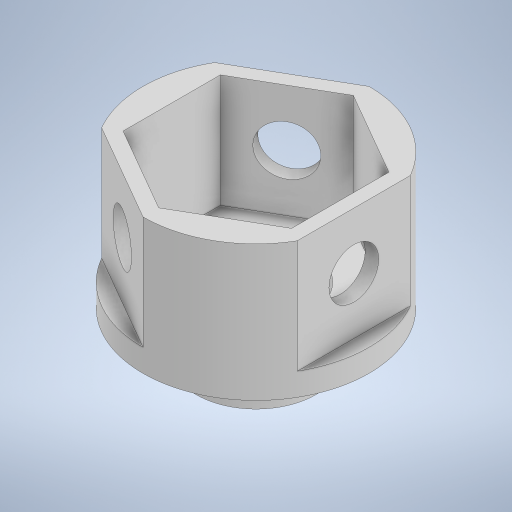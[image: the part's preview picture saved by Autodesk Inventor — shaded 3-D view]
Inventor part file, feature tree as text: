
AUTODESK INVENTOR PART (.ipt)
format: ipt  version: 2023 (Build 270158000, 158)  size: 289,792 bytes
history: native  units: in
note: dims shown in document units (in); Inventor stores cm internally (conversion verified against a paired STEP export)
features: extrude x7, sketch x7, pattern_circular x1
ambient origin geometry x8: Origin, YZ Plane, XZ Plane, XY Plane, X Axis, Y Axis, Z Axis, Center Point
bodies: Solid1 (feature_tree)
feature tree (15):
  extrude  "Extrusion1"  Depth=0.1969in TaperAngle=0.0deg
  extrude  "Extrusion2"  Depth=0.9843in TaperAngle=0.0deg
  extrude  "Extrusion3"  Depth=0.9843in TaperAngle=0.0deg
  extrude  "Extrusion4"  Depth=0.4921in
  extrude  "Extrusion5"  Depth=0.4921in
  pattern_circular  "Circular Pattern1"  Count=3 Angle=360.0deg
  extrude  "Extrusion6"  Depth=0.3937in
  extrude  "Extrusion7"  Depth=0.3937in
  sketch  "Sketch1"  dims[d0=1.9685in d1=0.1969in d2=0.0in]
  sketch  "Sketch2"  dims[d3=0.9843in d4=0.0in d5=0.9843in d6=0.0in]
  sketch  "Sketch3"  dims[d7=0.1181in d8=0.9843in d9=0.0in]
  sketch  "Sketch4"  dims[d10=0.4331in d11=0.4921in]
  sketch  "Sketch5"  dims[d12=0.4921in d13=0.4921in]
  sketch  "Sketch6"  dims[d14=0.4921in]
  sketch  "Sketch7"  dims[d15=0.9843in d16=0.0in d17=1.1811in d18=360.0deg d20=0.9449in d21=1.0394in d22=0.3937in d23=0.0in d24=0.3937in d25=0.0in]
